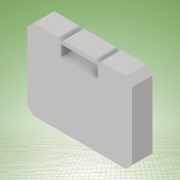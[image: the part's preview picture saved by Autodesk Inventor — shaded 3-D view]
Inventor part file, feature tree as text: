
AUTODESK INVENTOR PART (.ipt)
format: ipt  version: 2017 (Build 210142000, 142)  size: 130,048 bytes
history: native  units: in
note: dims shown in document units (in); Inventor stores cm internally (conversion verified against a paired STEP export)
features: extrude x1, chamfer x1, fillet x1, sketch x1
ambient origin geometry x8: Origin, YZ Plane, XZ Plane, XY Plane, X Axis, Y Axis, Z Axis, Center Point
bodies: Solid1 (feature_tree)
feature tree (4):
  extrude  "Extrusion1"  Depth=13.0in
  chamfer  "Chamfer1"  Distance=3.375in
  fillet  "Fillet1"  Radius=5.5in
  sketch  "Sketch1"  dims[d0=17.0in d1=13.0in d2=3.375in d3=0.0in d5=5.5in d6=5.5in d7=10.5in d11=1.0in d12=45.0deg d13=1.0in d14=0.125in d15=45.0deg d16=0.5in]
